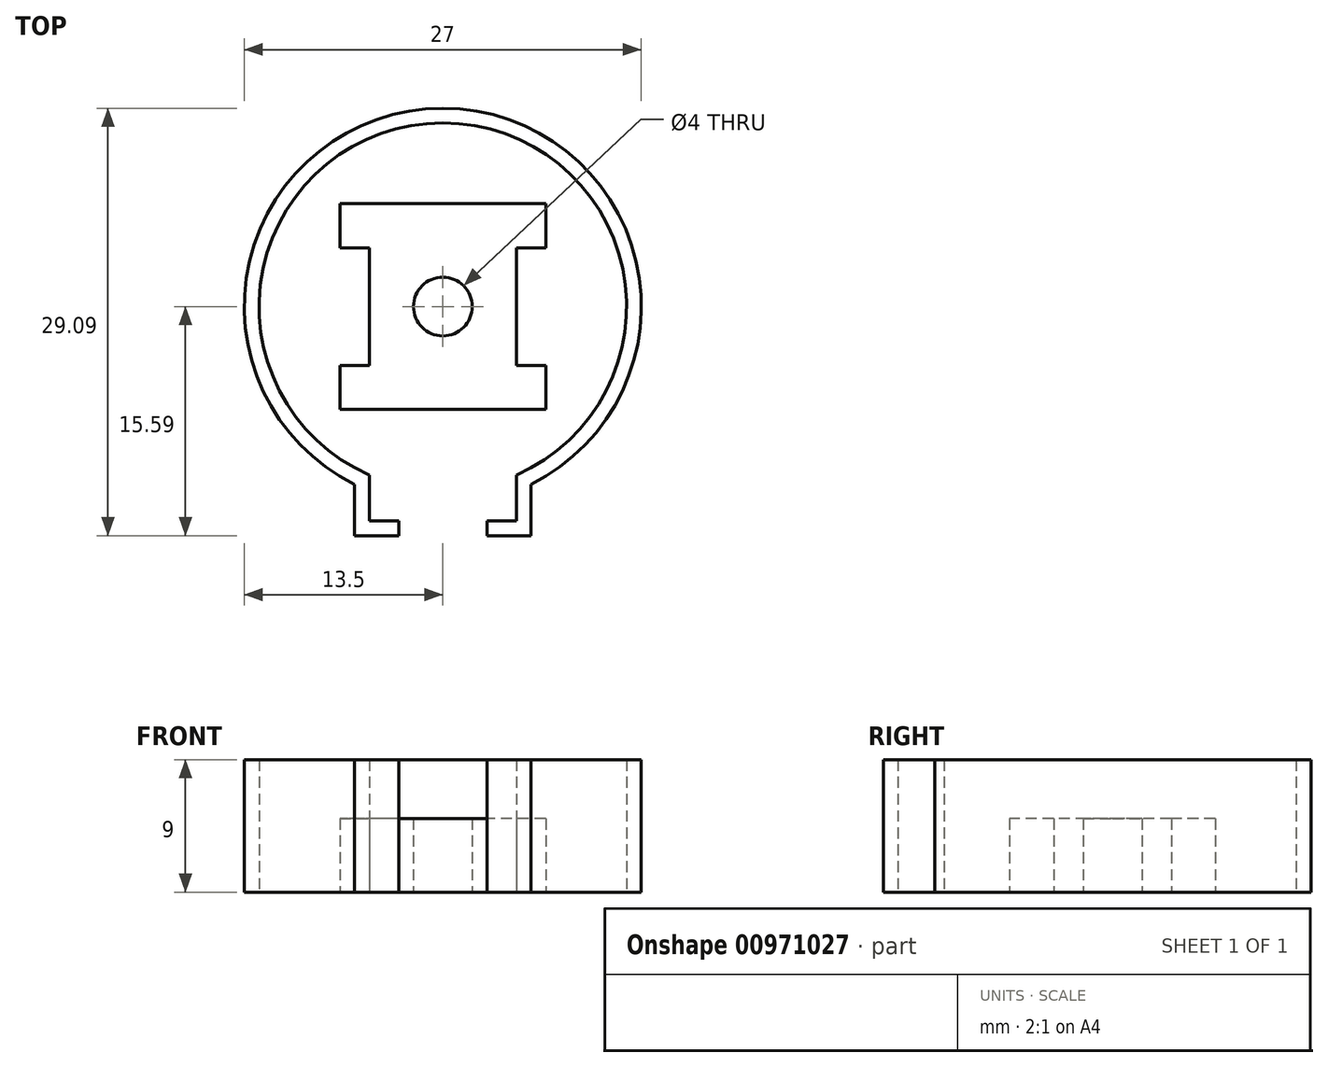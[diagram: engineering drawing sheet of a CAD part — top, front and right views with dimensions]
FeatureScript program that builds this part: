
annotation { "Feature Type Name" : "Feature", "Feature Type Description" : "" }
export const myFeature = defineFeature(function(context is Context, id is Id, definition is map)
    precondition{}
    {
        {
            var Q0;
            Q0=qCreatedBy(makeId("Top.planeOp"),FACE);
            var sketch = newSketch(context, id + "F0", { "sketchPlane" : qUnion([Q0])});
            skLineSegment(sketch, "E0.bottom", {"start": v(7, 7) * mm, "end": v(-7, 7) * mm});
            skLineSegment(sketch, "E0.top", {"start": v(7, -7) * mm, "end": v(-7, -7) * mm});
            skLineSegment(sketch, "E0.left", {"start": v(7, 7) * mm, "end": v(7, 4) * mm});
            skLineSegment(sketch, "E0.right", {"start": v(-7, 7) * mm, "end": v(-7, 4) * mm});
            skPoint(sketch, "E0.middle", {"position": v(0, 0) * mm});
            skCircle(sketch, "E1", {"center": v(0, 0) * mm, "radius": 2 * mm});
            skArc(sketch, "E2", {"start": v(5, -11.46) * mm, "mid": v(0, 12.5) * mm, "end": v(-5, -11.46) * mm});
            skLineSegment(sketch, "E3.bottom", {"start": v(-7, 4) * mm, "end": v(-5, 4) * mm});
            skLineSegment(sketch, "E3.top", {"start": v(-7, -4) * mm, "end": v(-5, -4) * mm});
            skLineSegment(sketch, "E3.right", {"start": v(-5, 4) * mm, "end": v(-5, -4) * mm});
            skPoint(sketch, "E3.middle", {"position": v(-6, 0) * mm});
            skPoint(sketch, "E3.middle.positionSnap0", {"position": v(-7, 0) * mm});
            skPoint(sketch, "E3.centerSnap0", {"position": v(-7, 0) * mm});
            skLineSegment(sketch, "E4.bottom", {"start": v(7, 4) * mm, "end": v(5, 4) * mm});
            skLineSegment(sketch, "E4.top", {"start": v(7, -4) * mm, "end": v(5, -4) * mm});
            skLineSegment(sketch, "E4.right", {"start": v(5, 4) * mm, "end": v(5, -4) * mm});
            skPoint(sketch, "E4.middle", {"position": v(6, 0) * mm});
            skLineSegment(sketch, "E5.trimOffspring", {"start": v(-7, -4) * mm, "end": v(-7, -7) * mm});
            skLineSegment(sketch, "E6.trimOffspring", {"start": v(7, -4) * mm, "end": v(7, -7) * mm});
            skLineSegment(sketch, "E7.right", {"start": v(-5, -11.46) * mm, "end": v(-5, -12.54) * mm});
            skPoint(sketch, "E7.middle", {"position": v(0, -13.5) * mm});
            skPoint(sketch, "E8.orphan", {"position": v(5, -16.4) * mm});
            skPoint(sketch, "E9.orphan", {"position": v(-5, -16.4) * mm});
            skPoint(sketch, "E10.orphan", {"position": v(5, -10.6) * mm});
            skPoint(sketch, "E11.orphan", {"position": v(-5, -10.6) * mm});
            skLineSegment(sketch, "E12.bottom", {"start": v(-5, -15.59) * mm, "end": v(-6, -15.59) * mm});
            skLineSegment(sketch, "E12.left", {"start": v(-5, -14.59) * mm, "end": v(-5, -11.46) * mm});
            skLineSegment(sketch, "E12.right", {"start": v(-6, -15.59) * mm, "end": v(-6, -12.1) * mm});
            skPoint(sketch, "E12.middle", {"position": v(-5.5, -12.33) * mm});
            skPoint(sketch, "E13.orphan", {"position": v(-5, -9.07) * mm});
            skPoint(sketch, "E14.orphan", {"position": v(-6, -9.07) * mm});
            skLineSegment(sketch, "E15.bottom", {"start": v(5, -15.59) * mm, "end": v(6, -15.59) * mm});
            skLineSegment(sketch, "E15.left", {"start": v(5, -14.59) * mm, "end": v(5, -11.46) * mm});
            skLineSegment(sketch, "E15.right", {"start": v(6, -15.59) * mm, "end": v(6, -12.1) * mm});
            skPoint(sketch, "E15.middle", {"position": v(5.5, -12.54) * mm});
            skPoint(sketch, "E15.top.end.orphan", {"position": v(6, -9.49) * mm});
            skPoint(sketch, "E15.top.start.orphan", {"position": v(5, -9.49) * mm});
            skArc(sketch, "E16.trimOffspring", {"start": v(6, -12.1) * mm, "mid": v(0, 13.5) * mm, "end": v(-6, -12.1) * mm});
            skPoint(sketch, "E17.start.orphan", {"position": v(5, -12.75) * mm});
            skLineSegment(sketch, "E18.bottom", {"start": v(-5, -15.59) * mm, "end": v(-3, -15.59) * mm});
            skLineSegment(sketch, "E18.top", {"start": v(-5, -14.59) * mm, "end": v(-3, -14.59) * mm});
            skLineSegment(sketch, "E18.right", {"start": v(-3, -15.59) * mm, "end": v(-3, -14.59) * mm});
            skLineSegment(sketch, "E19.bottom", {"start": v(5, -15.59) * mm, "end": v(3, -15.59) * mm});
            skLineSegment(sketch, "E19.top", {"start": v(5, -14.59) * mm, "end": v(3, -14.59) * mm});
            skLineSegment(sketch, "E19.right", {"start": v(3, -15.59) * mm, "end": v(3, -14.59) * mm});
            skSolve(sketch);
        }
        {
            var Q0;
            Q0=makeQuery(id+"F0.imprint","IMPRINT",FACE,{"disambiguationData":[TD([[makeQuery(id+"F0.imprint","IMPRINT",EDGE,{"derivedFrom":sQuery(id+"F0.wireOp",EDGE,"E0.bottom")}),1.0]])]});
            extrude(context, id + "F1", {"entities" : qUnion([Q0]), "depth" : 5 * mm, "offsetDistance" : 25 * mm});
        }
        {
            var Q0;
            {var subQ2=sQuery(id+"F0.wireOp",EDGE,"E2");Q0=makeQuery(id+"F0.imprint","IMPRINT",FACE,{"disambiguationData":[TD([[makeQuery(id+"F0.imprint","IMPRINT",EDGE,{"derivedFrom":subQ2}),-1.0]])]});}
            extrude(context, id + "F2", {"entities" : qUnion([Q0]), "depth" : 9 * mm, "offsetDistance" : 25 * mm});
        }
    });
